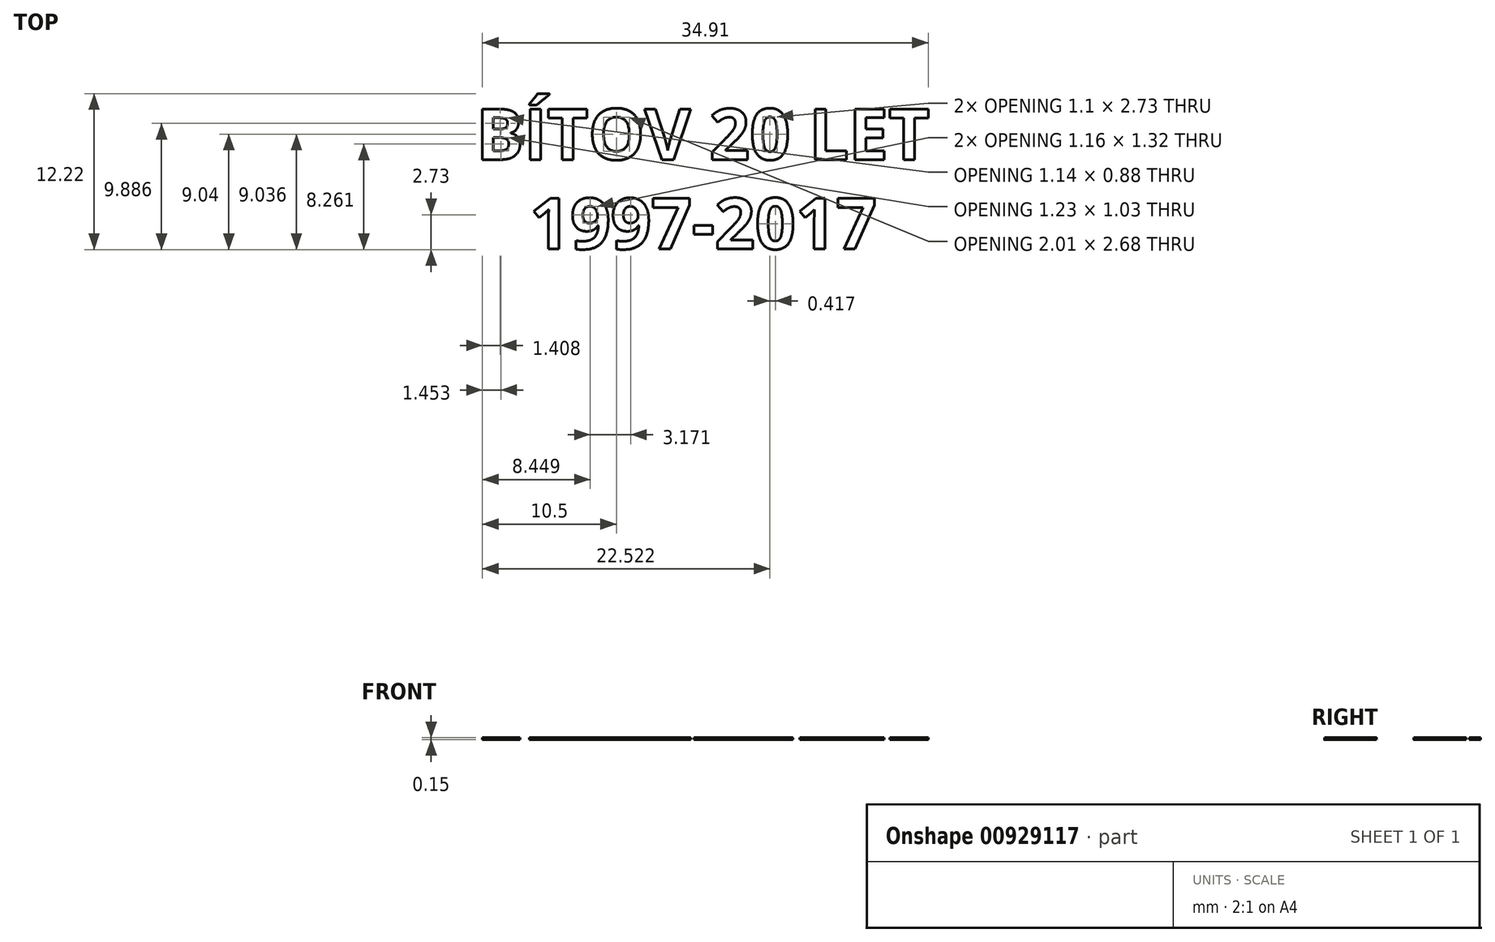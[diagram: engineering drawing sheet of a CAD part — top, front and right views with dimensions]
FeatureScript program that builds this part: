
annotation { "Feature Type Name" : "Feature", "Feature Type Description" : "" }
export const myFeature = defineFeature(function(context is Context, id is Id, definition is map)
    precondition{}
    {
        {
            var Q0;
            Q0=qCreatedBy(makeId("Top.planeOp"),FACE);
            var sketch = newSketch(context, id + "F0", { "sketchPlane" : qUnion([Q0])});
            skText(sketch, "E0", { "text": "BÍTOV 20 LET\n", "fontName": "OpenSans-Bold.ttf"});
            skText(sketch, "E1", { "text": "1997-2017", "fontName": "OpenSans-Bold.ttf"});
            const initialGuessF0  = {"E0": [-0.01788, 0, 1, 0, 0.004], "E1": [-0.01367, -0.007, 1, 0, 0.004]};
            skSetInitialGuess(sketch, initialGuessF0);
            skSolve(sketch);
        }
        {
            var Q0;
            Q0 = qSketchRegion(id + "F0", true);
            extrude(context, id + "F1", {"entities" : qUnion([Q0]), "depth" : 0.15 * mm, "offsetDistance" : 25 * mm});
        }
    });
